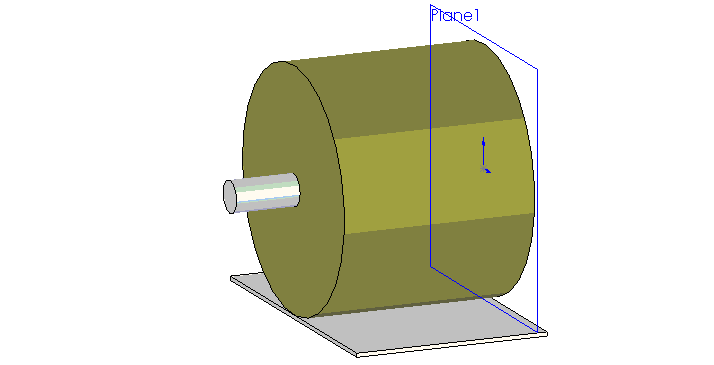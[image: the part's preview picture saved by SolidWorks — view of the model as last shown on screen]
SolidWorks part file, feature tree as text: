
SOLIDWORKS PART (.sldprt)
format: sldprt  version: not decoded by parser v0  size: 129,536 bytes
history: native  units: mm
features: sketch x3, extrude x3, plane x1 (+11 scaffold rows collapsed)
feature tree (18):
  scaffold x11  (default folders/planes/origin — collapsed)
  sketch  "Sketch1"  dims[D1=95.25mm]
  extrude  "Extrude1"  Depth=76.2mm
  sketch  "Sketch2"  dims[D1=12.7mm]
  extrude  "Extrude2"  Depth=25.4mm
  sketch  "Sketch3"  dims[D1=1.5875mm]
  plane  "Plane1"  Offset=76.2mm
  extrude  "Extrude3"  [1 undecoded]
decode coverage: 5 of 6 modeling features carry decoded parameters
note: 1 parameter value undecoded
note: suppression state not decoded; provenance and decode notes live in map.json
